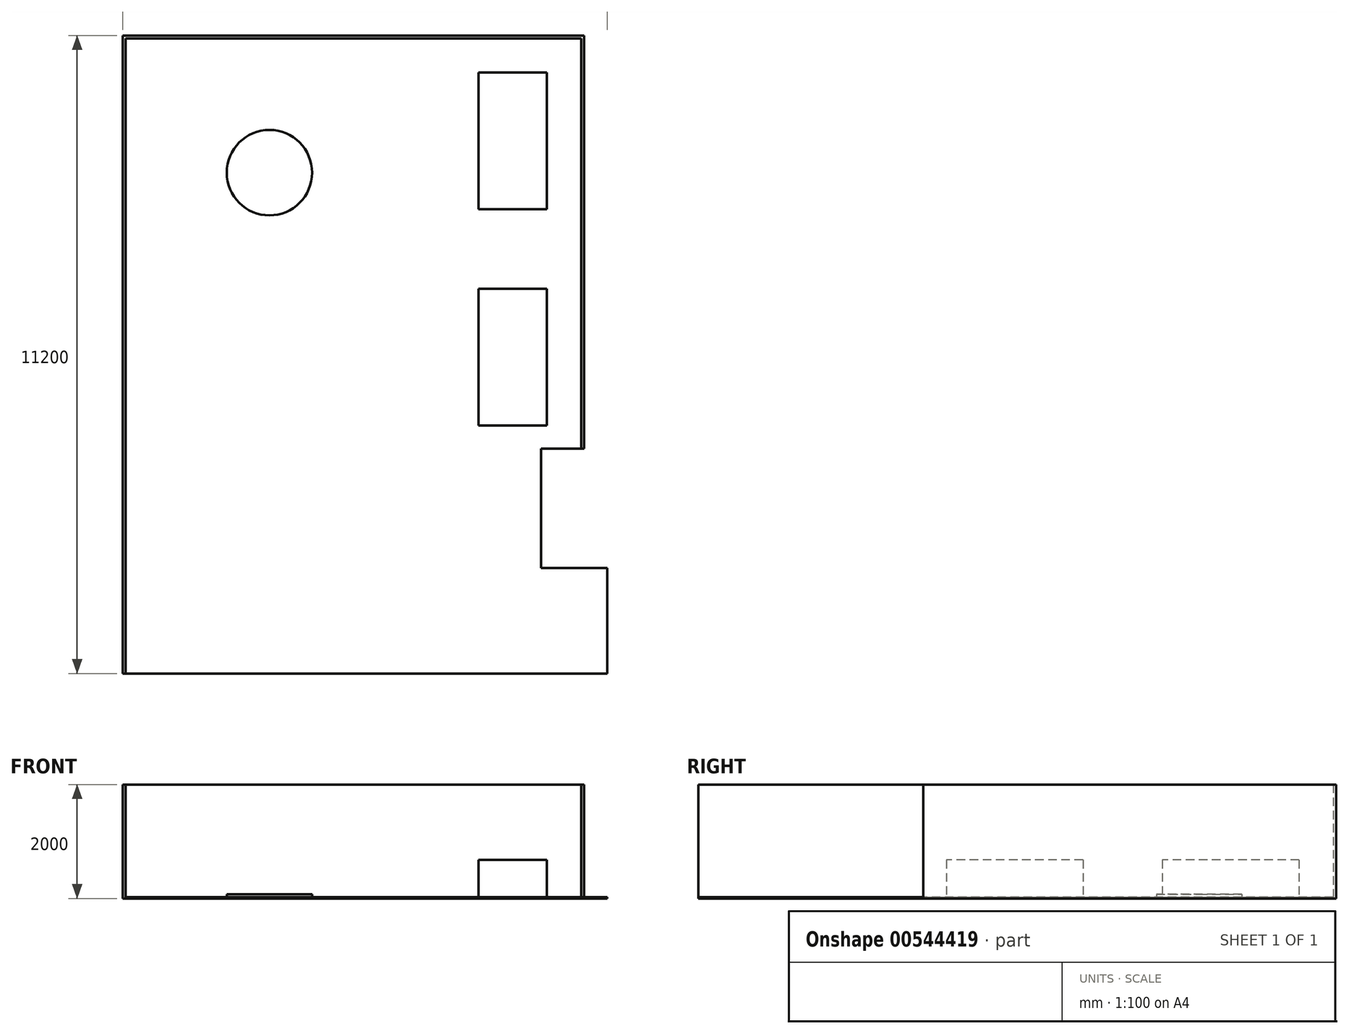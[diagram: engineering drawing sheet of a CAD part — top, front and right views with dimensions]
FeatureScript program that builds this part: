
annotation { "Feature Type Name" : "Feature", "Feature Type Description" : "" }
export const myFeature = defineFeature(function(context is Context, id is Id, definition is map)
    precondition{}
    {
        {
            var Q0;
            Q0=qCreatedBy(makeId("Top.planeOp"),FACE);
            var sketch = newSketch(context, id + "F0", { "sketchPlane" : qUnion([Q0])});
            skLineSegment(sketch, "E0", {"start": v(3786.2, -7247.04) * mm, "end": v(3786.2, -5397.04) * mm});
            skLineSegment(sketch, "E1", {"start": v(3786.2, -5397.04) * mm, "end": v(2626.2, -5397.04) * mm});
            skLineSegment(sketch, "E2", {"start": v(2626.2, -5397.04) * mm, "end": v(2626.2, -3297.04) * mm});
            skLineSegment(sketch, "E3", {"start": v(2626.2, -3297.04) * mm, "end": v(3326.2, -3297.04) * mm});
            skLineSegment(sketch, "E4", {"start": v(3326.2, -3297.04) * mm, "end": v(3326.2, 3902.96) * mm});
            skLineSegment(sketch, "E5", {"start": v(3326.2, 3902.96) * mm, "end": v(-4673.8, 3902.96) * mm});
            skLineSegment(sketch, "E6", {"start": v(-4673.8, 3902.96) * mm, "end": v(-4673.8, -7247.04) * mm});
            skLineSegment(sketch, "E7", {"start": v(-4673.8, -7247.04) * mm, "end": v(3786.2, -7247.04) * mm});
            skLineSegment(sketch, "E8.bottom", {"start": v(2726.2, 3302.96) * mm, "end": v(1526.2, 3302.96) * mm});
            skLineSegment(sketch, "E8.top", {"start": v(2726.2, 902.96) * mm, "end": v(1526.2, 902.96) * mm});
            skLineSegment(sketch, "E8.left", {"start": v(2726.2, 3302.96) * mm, "end": v(2726.2, 902.96) * mm});
            skLineSegment(sketch, "E8.right", {"start": v(1526.2, 3302.96) * mm, "end": v(1526.2, 902.96) * mm});
            skLineSegment(sketch, "E9.bottom", {"start": v(2726.2, -492.67) * mm, "end": v(1526.2, -492.67) * mm});
            skLineSegment(sketch, "E9.top", {"start": v(2726.2, -2892.67) * mm, "end": v(1526.2, -2892.67) * mm});
            skLineSegment(sketch, "E9.left", {"start": v(2726.2, -492.67) * mm, "end": v(2726.2, -2892.67) * mm});
            skLineSegment(sketch, "E9.right", {"start": v(1526.2, -492.67) * mm, "end": v(1526.2, -2892.67) * mm});
            skLineSegment(sketch, "E10", {"start": v(-4673.8, -7247.04) * mm, "end": v(-4723.8, -7247.04) * mm});
            skLineSegment(sketch, "E11", {"start": v(-4723.8, -7247.04) * mm, "end": v(-4723.8, 3952.96) * mm});
            skLineSegment(sketch, "E12", {"start": v(-4723.8, 3952.96) * mm, "end": v(3376.2, 3952.96) * mm});
            skLineSegment(sketch, "E13", {"start": v(3376.2, 3952.96) * mm, "end": v(3376.2, -3297.04) * mm});
            skLineSegment(sketch, "E14", {"start": v(3326.2, -3297.04) * mm, "end": v(3376.2, -3297.04) * mm});
            skSolve(sketch);
        }
        {
            var Q0;
            Q0=makeQuery(id+"F0.imprint","IMPRINT",FACE,{"disambiguationData":[TD([[makeQuery(id+"F0.imprint","IMPRINT",EDGE,{"derivedFrom":sQuery(id+"F0.wireOp",EDGE,"E9.bottom")}),1.0]])]});
            var Q1;
            Q1=makeQuery(id+"F0.imprint","IMPRINT",FACE,{"disambiguationData":[TD([[makeQuery(id+"F0.imprint","IMPRINT",EDGE,{"derivedFrom":sQuery(id+"F0.wireOp",EDGE,"E8.bottom")}),1.0]])]});
            var Q2;
            Q2=makeQuery(id+"F0.imprint","IMPRINT",FACE,{"disambiguationData":[TD([[makeQuery(id+"F0.imprint","IMPRINT",EDGE,{"derivedFrom":sQuery(id+"F0.wireOp",EDGE,"E0")}),1.0]])]});
            extrude(context, id + "F1", {"entities" : qUnion([Q0, Q1, Q2]), "depth" : 25 * mm, "offsetDistance" : 25 * mm});
        }
        {
            var Q0;
            Q0=makeQuery(id+"F0.imprint","IMPRINT",FACE,{"disambiguationData":[TD([[makeQuery(id+"F0.imprint","IMPRINT",EDGE,{"derivedFrom":sQuery(id+"F0.wireOp",EDGE,"E8.bottom")}),1.0]])]});
            var Q1;
            Q1=makeQuery(id+"F0.imprint","IMPRINT",FACE,{"disambiguationData":[TD([[makeQuery(id+"F0.imprint","IMPRINT",EDGE,{"derivedFrom":sQuery(id+"F0.wireOp",EDGE,"E9.bottom")}),1.0]])]});
            extrude(context, id + "F2", {"entities" : qUnion([Q0, Q1]), "depth" : 675 * mm, "offsetDistance" : 25 * mm});
        }
        {
            var Q0;
            Q0=makeQuery(id+"F0.imprint","IMPRINT",FACE,{"disambiguationData":[TD([[makeQuery(id+"F0.imprint","IMPRINT",EDGE,{"derivedFrom":sQuery(id+"F0.wireOp",EDGE,"E4")}),-1.0]])]});
            extrude(context, id + "F3", {"entities" : qUnion([Q0]), "depth" : 2000 * mm, "offsetDistance" : 25 * mm});
        }
        {
            var Q0;
            Q0=makeQuery(id+"F1.opExtrude","CAP_FACE",FACE,{"disambiguationData":[OSD([sQuery(id+"F0.wireOp",EDGE,"E0"),sQuery(id+"F0.wireOp",EDGE,"E1"),sQuery(id+"F0.wireOp",EDGE,"E2"),sQuery(id+"F0.wireOp",EDGE,"E3"),sQuery(id+"F0.wireOp",EDGE,"E4"),sQuery(id+"F0.wireOp",EDGE,"E5"),sQuery(id+"F0.wireOp",EDGE,"E6"),sQuery(id+"F0.wireOp",EDGE,"E7")])],"isStart":false});
            var sketch = newSketch(context, id + "F4", { "sketchPlane" : qUnion([Q0])});
            skCircle(sketch, "E15", {"center": v(-2147.22, 1545.19) * mm, "radius": 750 * mm});
            skSolve(sketch);
        }
        {
            var Q0;
            Q0=qSketchRegion(id+"F4",true);
            extrude(context, id + "F5", {"entities" : qUnion([Q0]), "depth" : 50 * mm, "offsetDistance" : 25 * mm});
        }
    });
